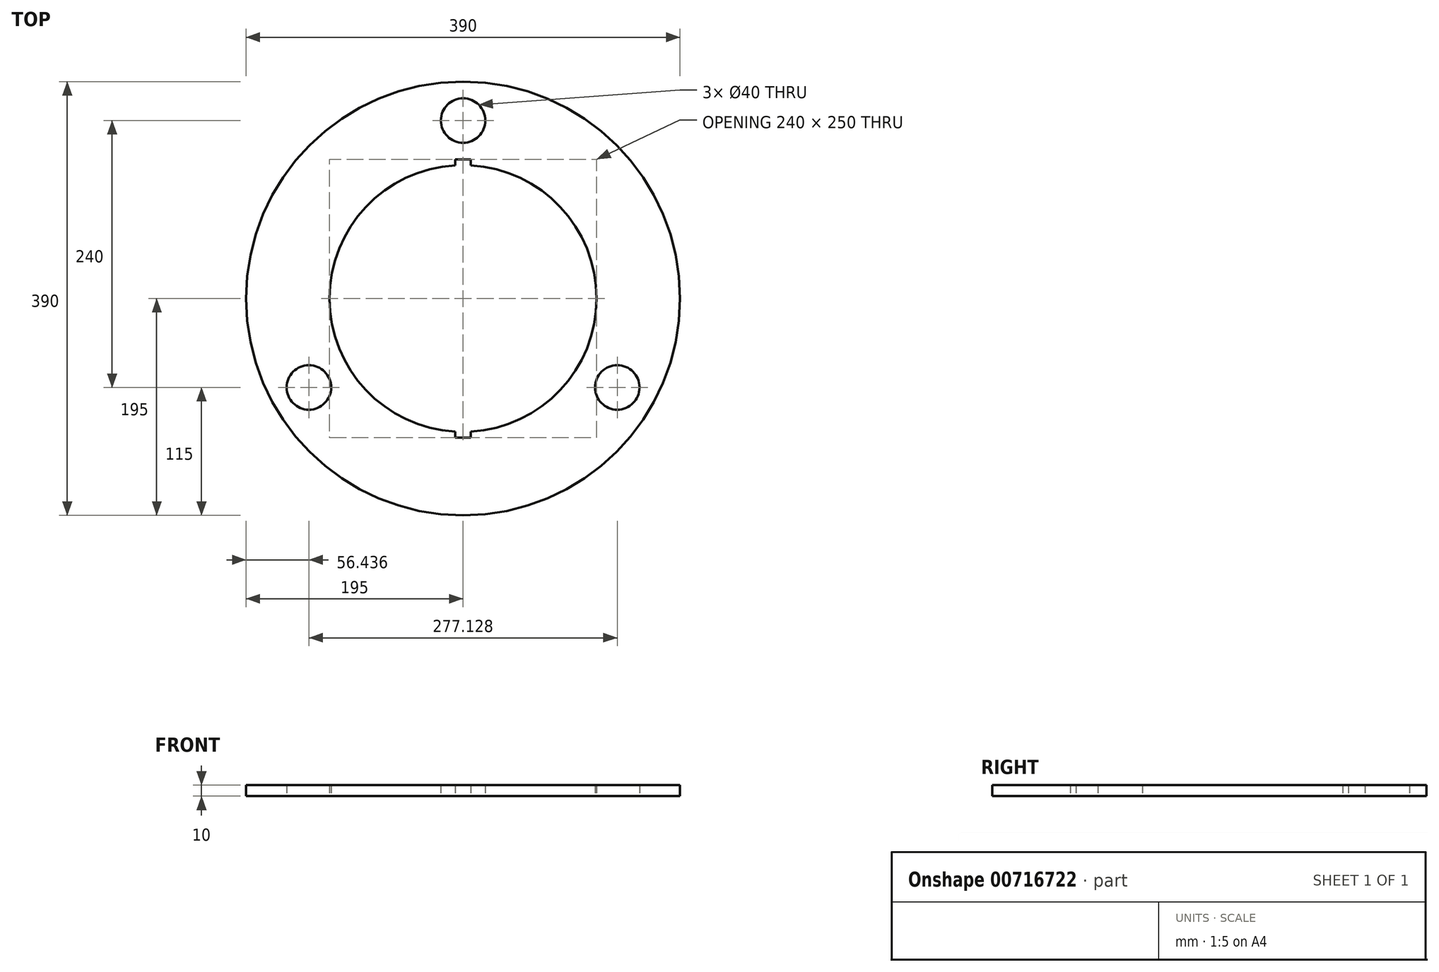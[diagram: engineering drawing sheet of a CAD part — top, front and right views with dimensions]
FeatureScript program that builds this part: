
annotation { "Feature Type Name" : "Feature", "Feature Type Description" : "" }
export const myFeature = defineFeature(function(context is Context, id is Id, definition is map)
    precondition{}
    {
        {
            var Q0;
            Q0=qCreatedBy(makeId("Top.planeOp"),FACE);
            var sketch = newSketch(context, id + "F0", { "sketchPlane" : qUnion([Q0])});
            skCircle(sketch, "E0", {"center": v(0, 0) * mm, "radius": 195 * mm});
            skCircle(sketch, "E1", {"center": v(0, 0) * mm, "radius": 120 * mm});
            skCircle(sketch, "E2", {"center": v(0, 160) * mm, "radius": 20 * mm});
            skCircle(sketch, "E3.1.0", {"center": v(-138.56, -80) * mm, "radius": 20 * mm});
            skCircle(sketch, "E3.2.0", {"center": v(138.56, -80) * mm, "radius": 20 * mm});
            skLineSegment(sketch, "E4.bottom", {"start": v(7, 115) * mm, "end": v(-7, 115) * mm});
            skLineSegment(sketch, "E4.top", {"start": v(7, 125) * mm, "end": v(-7, 125) * mm});
            skLineSegment(sketch, "E4.left", {"start": v(7, 115) * mm, "end": v(7, 125) * mm});
            skLineSegment(sketch, "E4.right", {"start": v(-7, 115) * mm, "end": v(-7, 125) * mm});
            skPoint(sketch, "E4.middle", {"position": v(0, 120) * mm});
            skLineSegment(sketch, "E5.1.0", {"start": v(-7, -115) * mm, "end": v(-7, -125) * mm});
            skLineSegment(sketch, "E5.1.1", {"start": v(7, -115) * mm, "end": v(7, -125) * mm});
            skPoint(sketch, "E5.1.2", {"position": v(0, -120) * mm});
            skLineSegment(sketch, "E5.1.3", {"start": v(-7, -125) * mm, "end": v(7, -125) * mm});
            skLineSegment(sketch, "E5.1.4", {"start": v(-7, -115) * mm, "end": v(7, -115) * mm});
            skSolve(sketch);
        }
        {
            var Q0;
            Q0=makeQuery(id+"F0.imprint","IMPRINT",FACE,{"disambiguationData":[TD([[makeQuery(id+"F0.imprint","IMPRINT",EDGE,{"derivedFrom":sQuery(id+"F0.wireOp",EDGE,"E0")}),1.0]])]});
            extrude(context, id + "F1", {"entities" : qUnion([Q0]), "depth" : 10 * mm, "offsetDistance" : 25 * mm});
        }
    });
